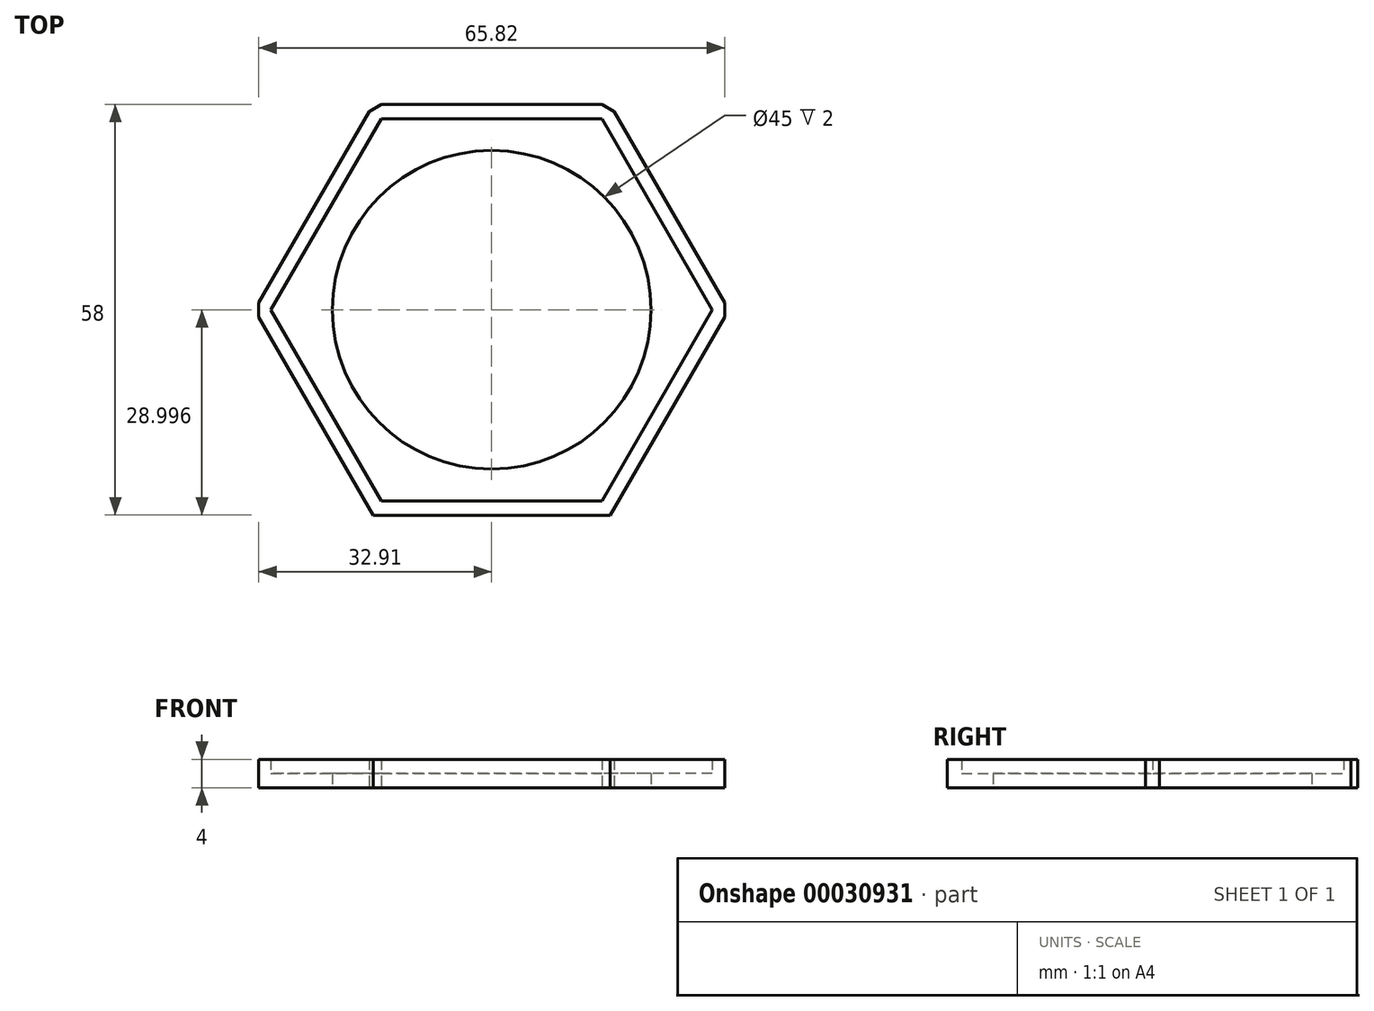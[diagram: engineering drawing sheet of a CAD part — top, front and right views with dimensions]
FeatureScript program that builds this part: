
annotation { "Feature Type Name" : "Feature", "Feature Type Description" : "" }
export const myFeature = defineFeature(function(context is Context, id is Id, definition is map)
    precondition{}
    {
        {
            var Q0;
            Q0=qCreatedBy(makeId("Top.planeOp"),FACE);
            var sketch = newSketch(context, id + "F0", { "sketchPlane" : qUnion([Q0])});
            skLineSegment(sketch, "E0.4", {"start": v(-80.59, -33.67) * mm, "end": v(-65, -6.67) * mm});
            skLineSegment(sketch, "E0.3", {"start": v(-65, -60.67) * mm, "end": v(-80.59, -33.67) * mm});
            skLineSegment(sketch, "E0.2", {"start": v(-33.82, -60.67) * mm, "end": v(-65, -60.67) * mm});
            skLineSegment(sketch, "E1", {"start": v(-32.67, -62.67) * mm, "end": v(-66.15, -62.67) * mm});
            skLineSegment(sketch, "E2", {"start": v(-66.15, -62.67) * mm, "end": v(-82.32, -34.67) * mm});
            skLineSegment(sketch, "E3.1", {"start": v(-66.73, -5.67) * mm, "end": v(-82.32, -32.67) * mm});
            skLineSegment(sketch, "E4.2", {"start": v(-33.82, -4.67) * mm, "end": v(-65, -4.67) * mm});
            skLineSegment(sketch, "E5.3", {"start": v(-16.5, -32.67) * mm, "end": v(-32.09, -5.67) * mm});
            skCircle(sketch, "E0.cCircle", {"center": v(-49.41, -33.67) * mm, "radius": 27 * mm, "construction": true});
            skLineSegment(sketch, "E0.0", {"start": v(-33.82, -6.67) * mm, "end": v(-18.23, -33.67) * mm});
            skCircle(sketch, "E6", {"center": v(-49.41, -33.67) * mm, "radius": 22.5 * mm});
            skLineSegment(sketch, "E0.5", {"start": v(-65, -6.67) * mm, "end": v(-33.82, -6.67) * mm});
            skLineSegment(sketch, "E7", {"start": v(-16.5, -34.67) * mm, "end": v(-32.67, -62.67) * mm});
            skLineSegment(sketch, "E0.1", {"start": v(-18.23, -33.67) * mm, "end": v(-33.82, -60.67) * mm});
            skLineSegment(sketch, "E8", {"start": v(-16.5, -34.67) * mm, "end": v(-16.5, -32.67) * mm});
            skLineSegment(sketch, "E9", {"start": v(-32.09, -5.67) * mm, "end": v(-33.82, -4.67) * mm});
            skLineSegment(sketch, "E10", {"start": v(-66.73, -5.67) * mm, "end": v(-65, -4.67) * mm});
            skLineSegment(sketch, "E11", {"start": v(-82.32, -34.67) * mm, "end": v(-82.32, -32.67) * mm});
            skSolve(sketch);
        }
        {
            var Q0;
            Q0=makeQuery(id+"F0.imprint","IMPRINT",FACE,{"disambiguationData":[TD([[makeQuery(id+"F0.imprint","IMPRINT",EDGE,{"derivedFrom":sQuery(id+"F0.wireOp",EDGE,"E0.4")}),-1.0]])]});
            extrude(context, id + "F1", {"entities" : qUnion([Q0]), "depth" : 2 * mm});
        }
        {
            var Q0;
            Q0=makeQuery(id+"F0.imprint","IMPRINT",FACE,{"disambiguationData":[TD([[makeQuery(id+"F0.imprint","IMPRINT",EDGE,{"derivedFrom":sQuery(id+"F0.wireOp",EDGE,"E0.4")}),1.0]])]});
            extrude(context, id + "F2", {"entities" : qUnion([Q0]), "operationType" : NewBodyOperationType.ADD, "depth" : 4 * mm});
        }
    });
